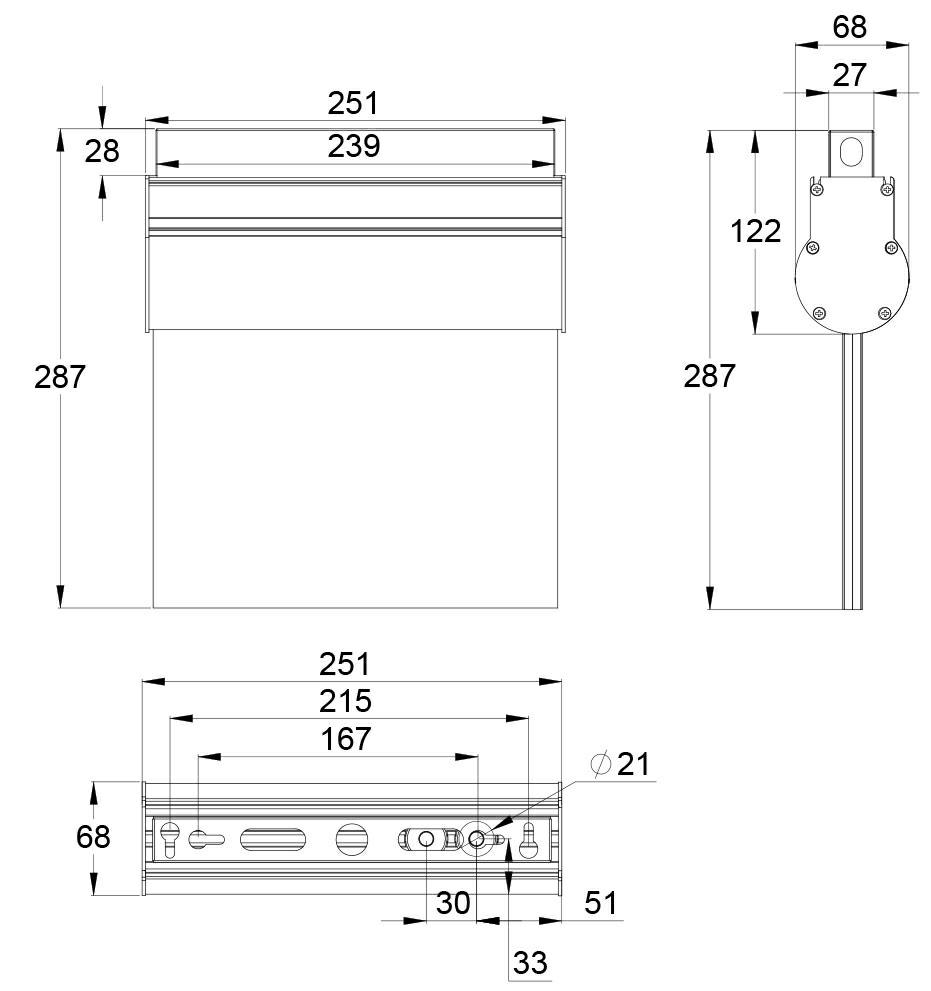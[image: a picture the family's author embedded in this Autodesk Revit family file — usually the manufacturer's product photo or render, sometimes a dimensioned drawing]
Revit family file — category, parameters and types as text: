
# Revit family: ESC 10 LED EMERGENCY EXIT LIGHT TWS8592W
name_source: partatom
category: Electrical Fixtures
revit_build: Autodesk Revit 2015 (Build: 20160512_0715(x64)
units: mm (PartAtom-declared; Revit-internal decimal feet)

## types (3) — shared parameters
Depth = 68 mm
Height = 259 mm  [stored 0.849738 ft]
Manufacturer = Teknoware Oy
Model = ESC 10 TWS85
Product Code = TWS8592W
Viewing Distance = 30000 mm  [stored 98.4252 ft]
Width = 324 mm  [stored 1.06299 ft]

## per-type parameters (varying)
| type | Back Pictogram | Down | Front Pictogram | Left | Right | Type Comments |
| -arrow right | Teknoware Pictogram PBV10301E left | No | Teknoware Pictogram PBV10301E right | No | Yes | PBV10301E |
| -arrow left | Teknoware Pictogram PBV10301E right | No | Teknoware Pictogram PBV10301E left | Yes | No | PBV10301E |
| -arrow down | Teknoware Pictogram PBV10302E | Yes | Teknoware Pictogram PBV10302E | No | No | PBV10302E |

note: [stored X ft] marks values corroborated as IEEE doubles in the binary element streams (Revit-internal decimal feet)

## geometry (parser evidence)
native form markers: Blend x8, Sweep x12
no freeform markers — native parametric forms only
